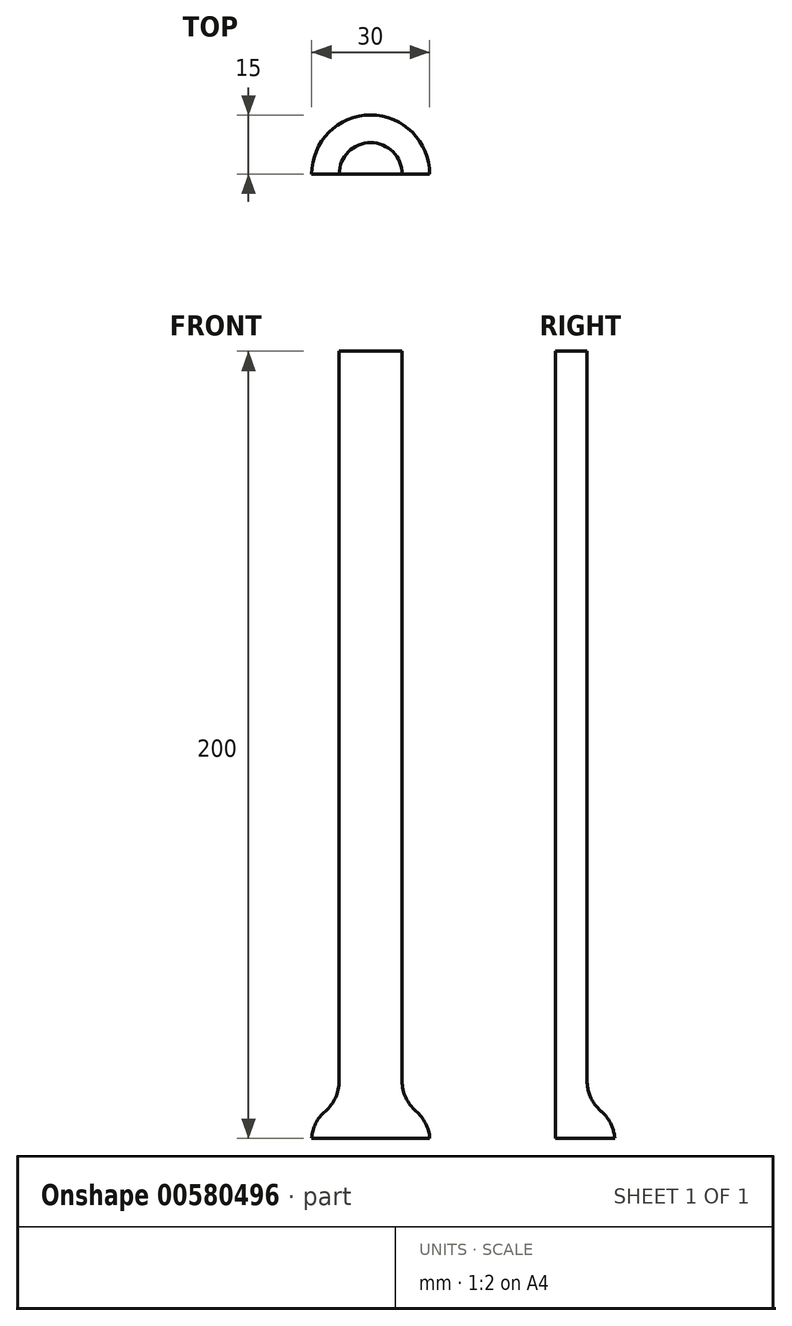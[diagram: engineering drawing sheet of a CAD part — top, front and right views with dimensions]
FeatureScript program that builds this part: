
annotation { "Feature Type Name" : "Feature", "Feature Type Description" : "" }
export const myFeature = defineFeature(function(context is Context, id is Id, definition is map)
    precondition{}
    {
        {
            var Q0;
            Q0=qCreatedBy(makeId("Top.planeOp"),FACE);
            var sketch = newSketch(context, id + "F0", { "sketchPlane" : qUnion([Q0])});
            skLineSegment(sketch, "E0", {"start": v(-15, 0) * mm, "end": v(15, 0) * mm});
            skArc(sketch, "E1", {"start": v(15, 0) * mm, "mid": v(0, 15) * mm, "end": v(-15, 0) * mm});
            skArc(sketch, "E2", {"start": v(8, 0) * mm, "mid": v(0, 8) * mm, "end": v(-8, 0) * mm});
            skSolve(sketch);
        }
        {
            var Q0;
            {var subQ0=sQuery(id+"F0.wireOp",EDGE,"E1");Q0=makeQuery(id+"F0.imprint","IMPRINT",FACE,{"disambiguationData":[TD([[makeQuery(id+"F0.imprint","IMPRINT",EDGE,{"derivedFrom":subQ0}),1.0]])]});}
            var Q1;
            {var subQ0=sQuery(id+"F0.wireOp",EDGE,"E2");Q1=makeQuery(id+"F0.imprint","IMPRINT",FACE,{"disambiguationData":[TD([[makeQuery(id+"F0.imprint","IMPRINT",EDGE,{"derivedFrom":subQ0}),1.0]])]});}
            extrude(context, id + "F1", {"entities" : qUnion([Q0, Q1]), "depth" : 5 * mm, "offsetDistance" : 25 * mm});
        }
        {
            var Q0;
            {var subQ0=sQuery(id+"F0.wireOp",EDGE,"E2");Q0=makeQuery(id+"F0.imprint","IMPRINT",FACE,{"disambiguationData":[TD([[makeQuery(id+"F0.imprint","IMPRINT",EDGE,{"derivedFrom":subQ0}),1.0]])]});}
            extrude(context, id + "F2", {"entities" : qUnion([Q0]), "operationType" : NewBodyOperationType.ADD, "depth" : 200 * mm, "offsetDistance" : 25 * mm});
        }
        {
            var Q0;
            Q0=makeQuery(id+"F2.boolean.opBoolean","INTERSECT",EDGE,{"derivedFrom":[makeQuery(id+"F1.opExtrude","CAP_FACE",FACE,{"disambiguationData":[OSD([sQuery(id+"F0.wireOp",EDGE,"E0"),sQuery(id+"F0.wireOp",EDGE,"E1")])],"isStart":false}),makeQuery(id+"F2.opExtrude","SWEPT_FACE",FACE,{"disambiguationData":[OSD([sQuery(id+"F0.wireOp",EDGE,"E2")])]})]});
            fillet(context, id + "F3", {"entities" : qUnion([Q0]), "radius" : 10 * mm, "tangentPropagation" : true, "allowEdgeOverflow" : false});
        }
        {
            var Q0;
            {var subQ0=sQuery(id+"F0.wireOp",EDGE,"E1");Q0=makeQuery(id+"F3.opFillet","BLEND_EDGE",EDGE,{"blendedFrom":[makeQuery(id+"F2.boolean.opBoolean","INTERSECT",EDGE,{"derivedFrom":[makeQuery(id+"F1.opExtrude","CAP_FACE",FACE,{"disambiguationData":[OSD([sQuery(id+"F0.wireOp",EDGE,"E0"),subQ0])],"isStart":false}),makeQuery(id+"F2.opExtrude","SWEPT_FACE",FACE,{"disambiguationData":[OSD([sQuery(id+"F0.wireOp",EDGE,"E2")])]})]}),makeQuery(id+"F1.opExtrude","SWEPT_FACE",FACE,{"disambiguationData":[OSD([subQ0])]})],"blendedInto":[makeQuery(id+"F1.opExtrude","SWEPT_FACE",FACE,{"disambiguationData":[OSD([subQ0])]})]});}
            fillet(context, id + "F4", {"entities" : qUnion([Q0]), "radius" : 10 * mm, "tangentPropagation" : true, "allowEdgeOverflow" : false});
        }
    });
